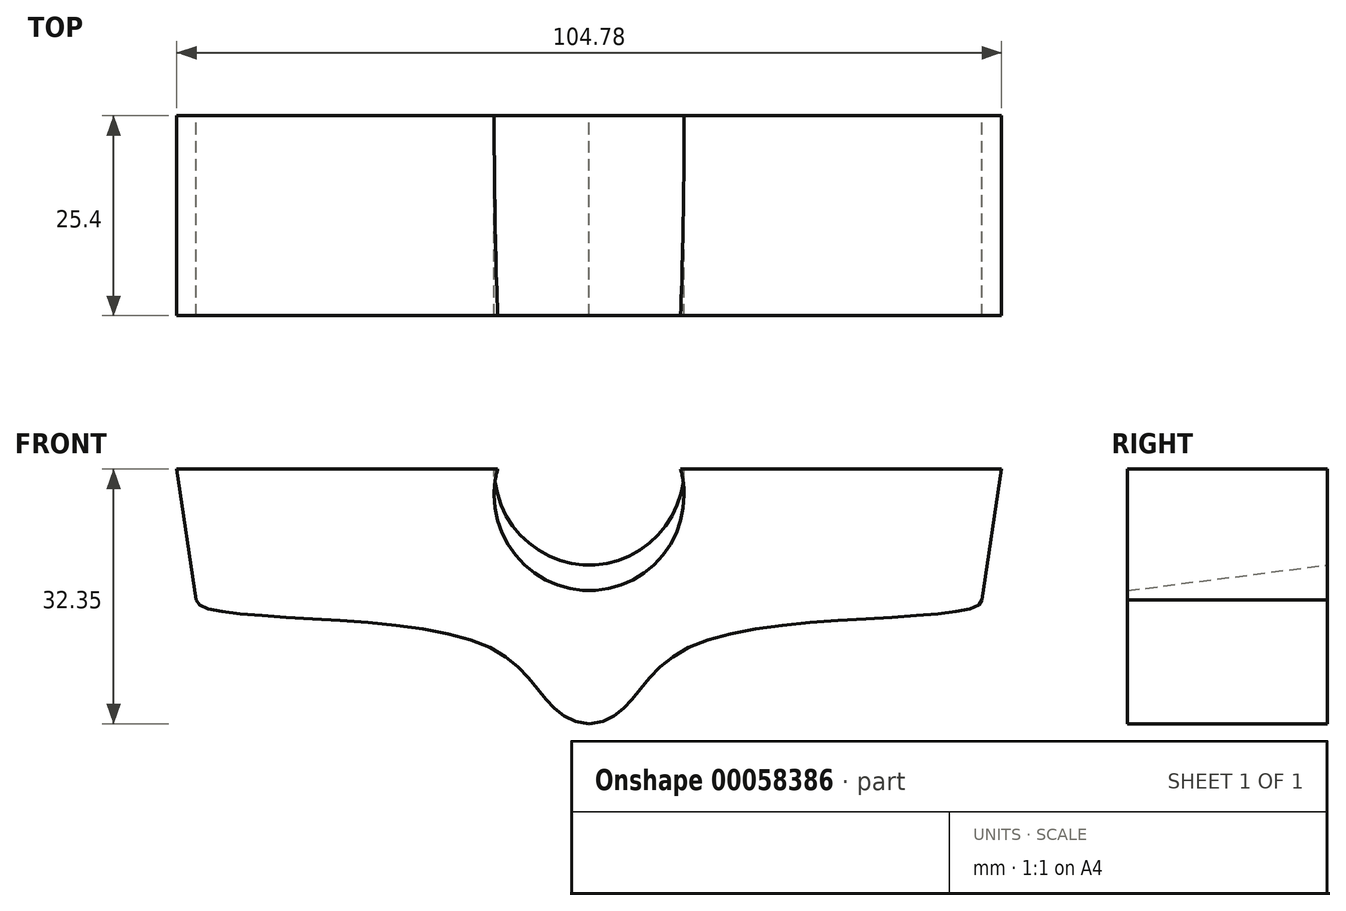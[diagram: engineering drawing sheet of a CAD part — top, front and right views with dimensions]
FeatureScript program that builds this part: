
annotation { "Feature Type Name" : "Feature", "Feature Type Description" : "" }
export const myFeature = defineFeature(function(context is Context, id is Id, definition is map)
    precondition{}
    {
        {
            var Q0;
            Q0=qCreatedBy(makeId("Front.planeOp"),FACE);
            var sketch = newSketch(context, id + "F0", { "sketchPlane" : qUnion([Q0])});
            skPoint(sketch, "E0.orphan", {"position": v(0, 67.17) * mm});
            skLineSegment(sketch, "E1", {"start": v(-52.39, 0) * mm, "end": v(52.39, 0) * mm});
            skPoint(sketch, "E2.end.orphan", {"position": v(0, -32.35) * mm});
            skPoint(sketch, "E3.start.orphan", {"position": v(0, -28.43) * mm});
            skLineSegment(sketch, "E4", {"start": v(-52.39, 0) * mm, "end": v(-49.9, -16.6) * mm});
            skLineSegment(sketch, "E5", {"start": v(-49.9, -16.6) * mm, "end": v(-49.9, -16.6) * mm});
            skFitSpline(sketch, "E6", {"points": [v(-49.9, -16.6) * mm, v(-12.9, -22.52) * mm, v(0, -32.35) * mm], "startDerivative": vector(0, -16.61) * mm, "endDerivative": vector(44.56, -2.38) * mm});
            skLineSegment(sketch, "E7.MirrorCS", {"start": v(52.39, 0) * mm, "end": v(49.9, -16.6) * mm});
            skFitSpline(sketch, "E8.MirrorCS", {"points": [v(49.9, -16.6) * mm, v(12.9, -22.52) * mm, v(0, -32.35) * mm], "startDerivative": vector(0, -16.61) * mm, "endDerivative": vector(-44.56, -2.38) * mm});
            skLineSegment(sketch, "E9.MirrorCS", {"start": v(49.9, -16.6) * mm, "end": v(49.9, -16.6) * mm});
            skSolve(sketch);
        }
        {
            var Q0;
            Q0 = qSketchRegion(id + "F0", true);
            extrude(context, id + "F1", {"entities" : qUnion([Q0]), "depth" : 25.4 * mm});
        }
        {
            var Q0;
            Q0=makeQuery(id+"F1.opExtrude","CAP_EDGE",EDGE,{"disambiguationData":[OSD([sQuery(id+"F0.wireOp",EDGE,"E1")])],"isStart":true});
            var Q1;
            Q1=qCreatedBy(makeId("Front.planeOp"),FACE);
            cPlane(context, id + "F2", {"entities" : qUnion([Q0, Q1]), "cplaneType" : CPlaneType.LINE_ANGLE, "offset" : 152.4 * mm, "angle" : 7.3 * degree, "width" : 152.4 * mm, "height" : 152.4 * mm});
        }
        {
            var Q0;
            Q0=qCreatedBy(id+"F2.planeOp",FACE);
            var sketch = newSketch(context, id + "F3", { "sketchPlane" : qUnion([Q0])});
            skCircle(sketch, "E10", {"center": v(0, 0) * mm, "radius": 12.07 * mm});
            skSolve(sketch);
        }
        {
            var Q0;
            Q0 = qSketchRegion(id + "F3", true);
            extrude(context, id + "F4", {"entities" : qUnion([Q0]), "operationType" : NewBodyOperationType.REMOVE, "oppositeDirection" : true, "depth" : 76.2 * mm});
        }
    });
